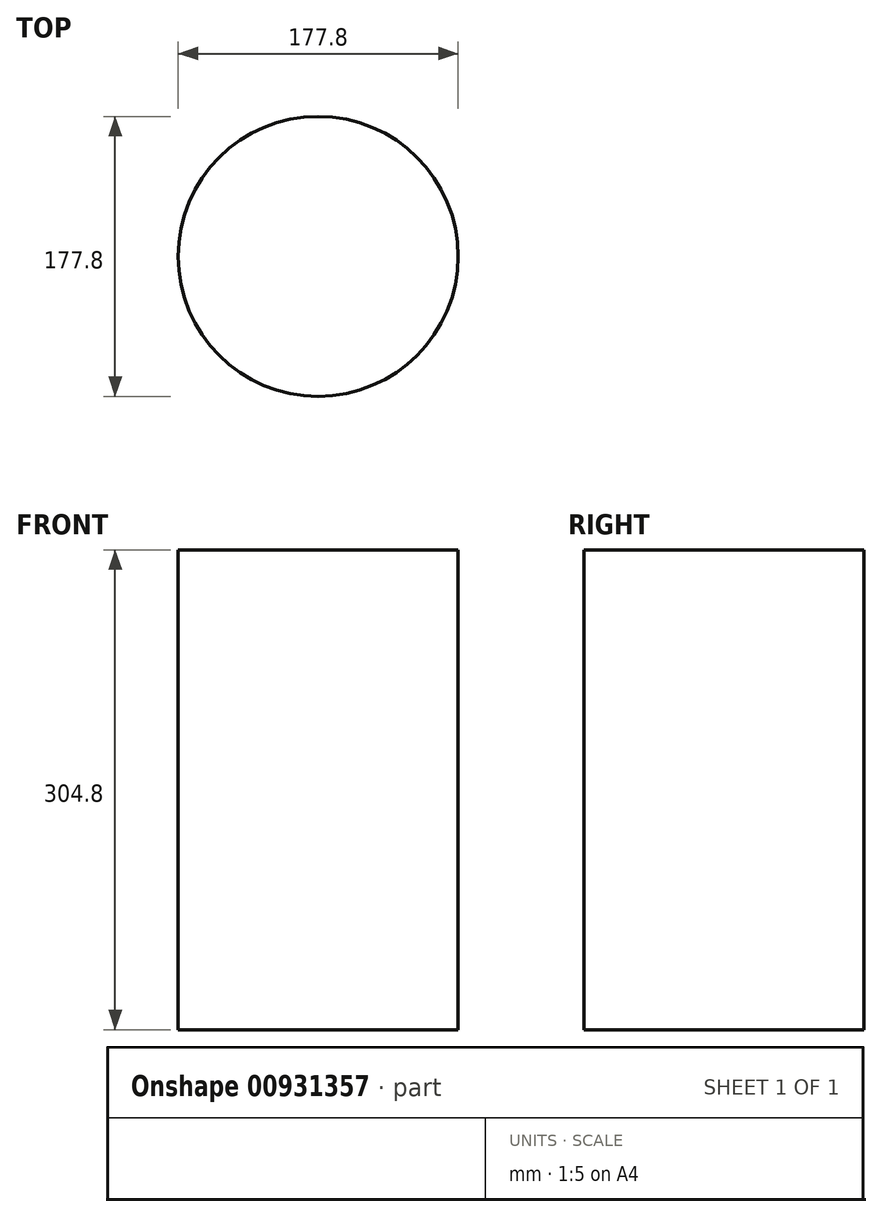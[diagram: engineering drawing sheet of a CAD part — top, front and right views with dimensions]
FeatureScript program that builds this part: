
annotation { "Feature Type Name" : "Feature", "Feature Type Description" : "" }
export const myFeature = defineFeature(function(context is Context, id is Id, definition is map)
    precondition{}
    {
        {
            var Q0;
            Q0=qCreatedBy(makeId("Top.planeOp"),FACE);
            var sketch = newSketch(context, id + "F0", { "sketchPlane" : qUnion([Q0])});
            skCircle(sketch, "E0", {"center": v(110.34, 177.15) * mm, "radius": 88.9 * mm});
            skSolve(sketch);
        }
        {
            var Q0;
            Q0 = qSketchRegion(id + "F0", true);
            extrude(context, id + "F1", {"entities" : qUnion([Q0]), "depth" : 304.8 * mm, "offsetDistance" : 25.4 * mm});
        }
    });
